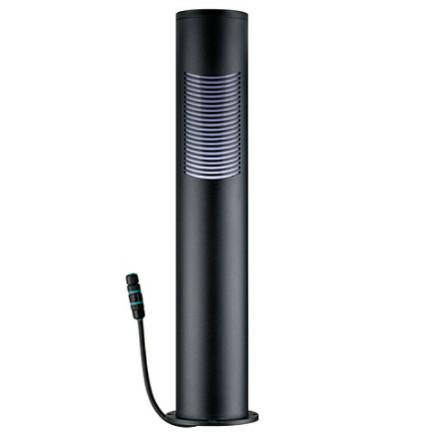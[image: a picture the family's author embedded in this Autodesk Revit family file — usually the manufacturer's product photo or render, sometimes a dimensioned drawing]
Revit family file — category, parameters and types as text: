
# Revit family: GALAD Столбик LED
name_source: partatom
category: Осветительные приборы
revit_build: Autodesk Revit 2018 (Build: 20180423_1000(x64)
units: mm (PartAtom-declared; Revit-internal decimal feet)

## family parameters
Источник света = Да
Общий = Нет
Основа = Грань
При загрузке вырезать с полостями = Нет
Размер круглого соединителя = Использовать диаметр
Тип детали = Нормальный
Точка расчета площади = Нет

## types (2) — shared parameters
ADSK_Версия Revit = 2018
ADSK_Версия семейства = 1.01
ADSK_Единица измерения = шт.
ADSK_Завод-изготовитель = Лихославльский завод 'Светотехника'
ADSK_Классификация нагрузок = Освещение
ADSK_Количество = 1
ADSK_Количество фаз = 1
ADSK_Коэффициент мощности = 0.9
ADSK_Масса = 5
ADSK_Масса_Текст = 5
ADSK_Напряжение = 230 В
ADSK_Номинальная мощность = 9 В·А
ADSK_Обозначение = ГОСТ IEC 60598-1, ГОСТ 17516.1, ГОСТ 15150
ADSK_Полная мощность = 10 В·А
ADSK_Размер_Высота = 695 мм
ADSK_Размер_Длина = 125 мм
ADSK_Размер_Ширина = 125 мм
ADSK_Ток = 0 А
ADSK_Энергоэффективность = 3 лм/Вт
IP = 54
URL = https://galad.ru
Блок аварийного питания = Нет
Возможный угол наклона = 0
Диапазон цветовой температуры = 5028±283
Изготовитель = Лихославльский завод 'Светотехника'
Класс Защиты = 1
Класс защиты от поражения электрическим током = 1
Класс светораспределения = П
Климатическая зона = У1
Климатическое исполнение = -45...40 °С
Коэффициент пульсации = менее 5%
Материал корпуса = Литой алюминий
Материал рассеивателя = ПММА
Область использования = Садово-парковое освещение
Описание = GALAD Столбик LED - стильный ландшафтный светильник, с помощью которого можно создать уютную атмосферу в тихих уголках современного города. Мягкий свет, прочная антивандальная конструкция, устойчивость к погодным условиям.
Отметка по умолчанию = 1219 мм
Полная установленная мощность = 10 В·А
Световая отдача = 3
Светофильтр = 16777215
Смещение цветовой температуры при затухании лампы = <Нет>
Снижение светового потока во время разгорания = не более 6%
Срок службы = 12 лет
Тип ПРА = ЭПРА
Тип источника света = LED
Тип монтажной поверхности = садово-парковая территория
Тип продукции = Светильник
Тип устройства управления светодиодами = без управления
Угол наклона = -90.00°
Цветопередача = 70
Частота = 50
zero-valued in all types: Неравномерность яркости

## per-type parameters (varying)
| type | ADSK_Код изделия | ADSK_Наименование краткое | Файл фотометрической сетки |
| GALAD Столбик LED-9 (30/750/700/RAL9005/0/GEN1) | 13792 | GALAD Столбик LED-9 | stolbik LED-9 (750_700_RAL9005_0_GEN1).IES |
| GALAD Столбик LED-9 (30/750/700/RAL9005/0/TW/GEN1) | 15640 | GALAD Столбик LED-9 TW | stolbik LED-9 (750_700_RAL9005_0_TW_GEN1).IES |

note: column(s) folded — value = type name in every type: ADSK_Марка, ADSK_Наименование
